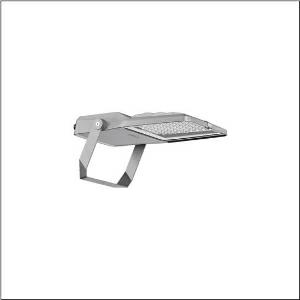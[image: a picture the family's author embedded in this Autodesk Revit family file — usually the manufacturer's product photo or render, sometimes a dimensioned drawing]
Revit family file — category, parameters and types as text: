
# Revit family: floodlight_fl_21_mini___pl64_5xa7771c4e1a_c03f
name_source: partatom
category: Lighting Fixtures
units: mm (PartAtom-declared; Revit-internal decimal feet)

## family parameters
Cut with Voids When Loaded = No
Host = Face
Light Source = No
Part Type = Normal
Room Calculation Point = No
Round Connector Dimension = Use Diameter
Shared = No

## types (1)
- --- (1 x LED, 12280 lm, 87.2 W, 4000K)
    Apparent Load = 87 VA
    CIE Flux Codes = 28 80 98 100 100
    Color Rendering = 70
    Color Temperature = 4000K
    Default Elevation = 1800 mm
    Description = Floodlight FL 21 mini, floodlight, primary light control with lens, of PMMA, primary optical cover: protective disc, of toughened safety glass, transparent, light distribution: PL64, light emission: direct distribution, installation type: surface-mounted, LED, High Power LED, rated luminous flux: 12.280lm, luminous efficacy: 141lm/W, light colour: 740, colour temperature: 4000K, control gear: ECG iQ, control: Auto-Match, Temp-Guard, Lumen-Switch, Night-Set, Smart-Wire, Light-Fading, Desk-Remote (wireless, voltage-free reading and setting of iQ features in the workshop via application-optimized NFC function/RFID function), optimised constant luminous flux control (CLO 2.0), with terminal, 6-pole, mains connection: 220..240V, AC, 50/60Hz, start of lifetime: 87W, end of lifetime: 92W, reduction: 40W, luminaire housing, of diecast aluminium, powder-coated, Siteco® metallic grey (DB 702S), corrosivity category C5 according to DIN EN ISO 12944, mounting bracket, of steel, galvanised, powder-coated, Siteco® metallic grey (DB 702S), protection rating (complete): IP66, insulation class (complete): insulation class II (safety insulation), certification: CE, ENEC, VDE, protection symbol: D, impact resistance: IK08, permissible operating ambient temperature: -40..+40°C, permissible operating ambient temperature for outdoor applications: -40..+50°C, standard: DIN EN 12944, packaging unit: 1 piece

Light Distribution: PL64
    Height = 70 mm
    Lamp = 1 x LED
    Lamp Light Flux = 12280 lm
    Lamp Power = 87.2 W
    Lamp count = 1
    Length = 485 mm
    Luminous efficacy = 141 lm/W
    Manufacturer = Siteco
    ModVariant = No
    Model = 5XA7771C4E1A
    Number of Poles = 1
    OnlyDefault = Yes
    Power Factor = 1
    Product Name = Floodlight FL 21 mini | PL64
    Product group = floodlight | pylon top
    ProductGroupID = 6101
    Protection Class = Protection class II
    Protection Degree = IP 66
    RLX_Detail_Level = 1
    RlxData = <blob elided: 96265 chars, md5=67580eb8>
    Socket = socket
    Standby Power = 0 W
    System Light Flux = 12280 lm
    System Power = 87 W
    Type Comments = factory setting: luminous flux: 100 % | dim-lin: 254 | 456 mA
    Type Image = l_1006845.jpg
    URL = http://relux.com
    VarID = @adj_077629
    Voltage = 0 V
    Weight = 0.00 kg
    Width = 337 mm

## geometry (parser evidence)
native form markers: Blend x4, Sweep x12
no freeform markers — native parametric forms only
